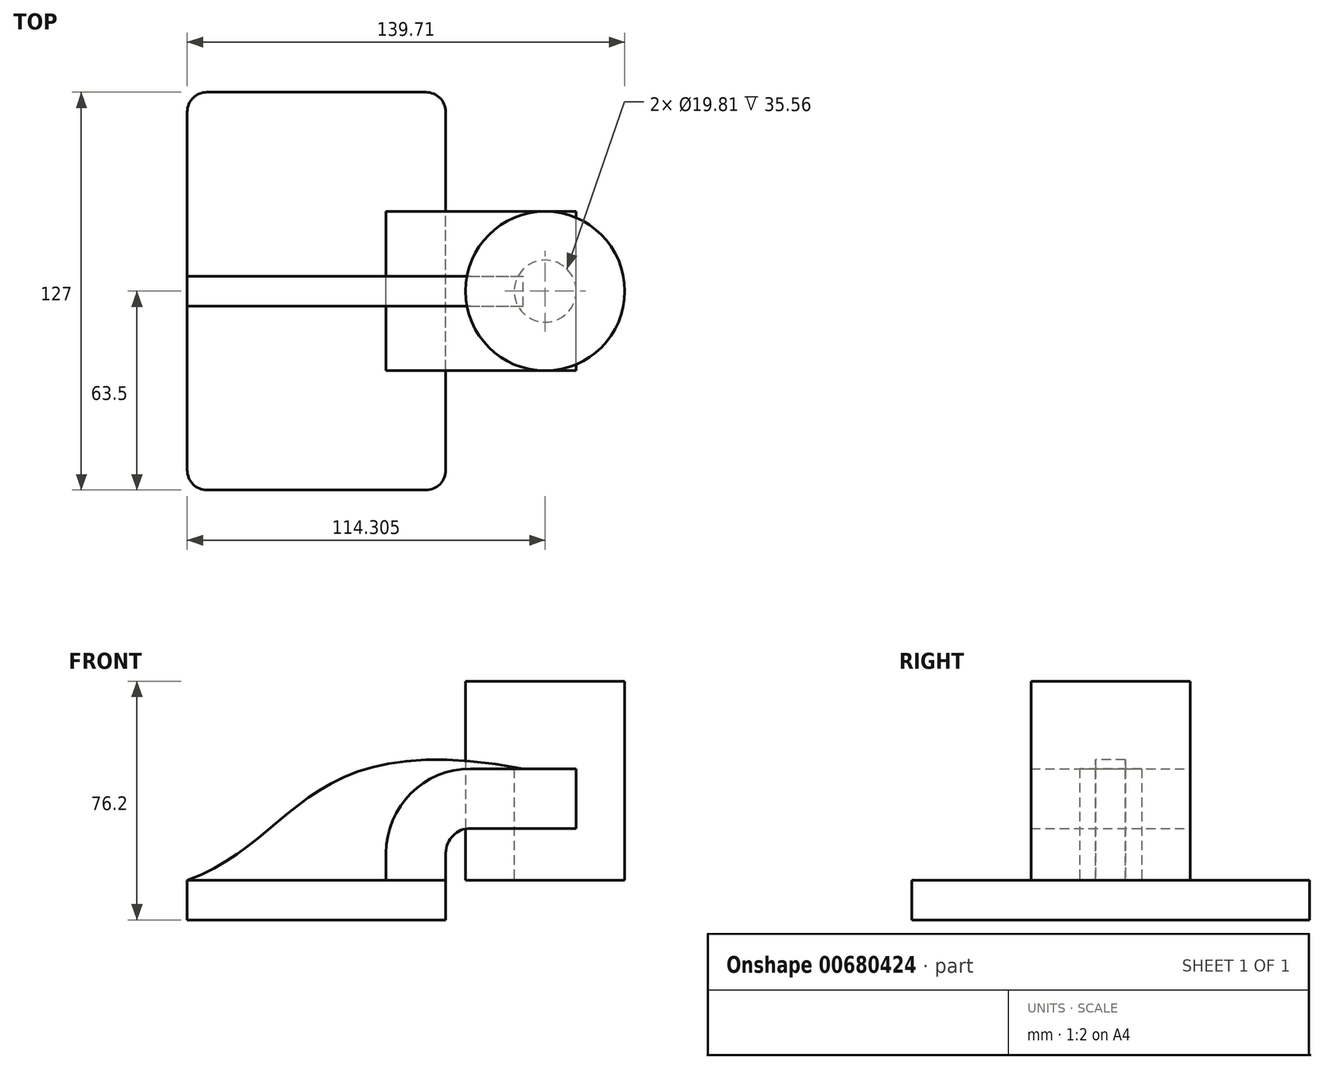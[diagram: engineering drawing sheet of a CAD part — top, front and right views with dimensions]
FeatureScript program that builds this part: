
annotation { "Feature Type Name" : "Feature", "Feature Type Description" : "" }
export const myFeature = defineFeature(function(context is Context, id is Id, definition is map)
    precondition{}
    {
        {
            var Q0;
            Q0=qCreatedBy(makeId("Front.planeOp"),FACE);
            var sketch = newSketch(context, id + "F0", { "sketchPlane" : qUnion([Q0])});
            skLineSegment(sketch, "E0.bottom", {"start": v(41.27, 6.35) * mm, "end": v(-41.28, 6.35) * mm});
            skLineSegment(sketch, "E0.top", {"start": v(41.28, -6.35) * mm, "end": v(-41.27, -6.35) * mm});
            skLineSegment(sketch, "E0.left", {"start": v(41.28, 6.35) * mm, "end": v(41.28, -6.35) * mm});
            skLineSegment(sketch, "E0.right", {"start": v(-41.28, 6.35) * mm, "end": v(-41.27, -6.35) * mm});
            skPoint(sketch, "E0.middle", {"position": v(0, 0) * mm});
            skLineSegment(sketch, "E1.bottom", {"start": v(98.42, 6.35) * mm, "end": v(73.03, 6.35) * mm});
            skLineSegment(sketch, "E1.top", {"start": v(98.42, 69.85) * mm, "end": v(73.02, 69.85) * mm});
            skLineSegment(sketch, "E1.left", {"start": v(98.42, 6.35) * mm, "end": v(98.42, 69.85) * mm});
            skLineSegment(sketch, "E1.right", {"start": v(73.03, 6.35) * mm, "end": v(73.03, 69.85) * mm});
            skPoint(sketch, "E1.middle", {"position": v(85.72, 38.1) * mm});
            skLineSegment(sketch, "E2", {"start": v(41.27, 6.35) * mm, "end": v(41.27, 14.95) * mm});
            skArc(sketch, "E3", {"start": v(49.18, 22.86) * mm, "mid": v(43.6, 20.54) * mm, "end": v(41.27, 14.95) * mm});
            skLineSegment(sketch, "E4", {"start": v(49.18, 22.86) * mm, "end": v(82.93, 22.86) * mm});
            skArc(sketch, "E5.1", {"start": v(49.18, 41.91) * mm, "mid": v(30.12, 34.01) * mm, "end": v(22.22, 14.95) * mm});
            skLineSegment(sketch, "E5.2", {"start": v(49.18, 41.91) * mm, "end": v(82.93, 41.91) * mm});
            skFitSpline(sketch, "E6", {"points": [v(-41.28, 6.35) * mm, v(66.06, 41.91) * mm], "startDerivative": vector(107.33, 38.1) * mm, "endDerivative": vector(213.02, -39.97) * mm});
            skLineSegment(sketch, "E7", {"start": v(22.22, 14.95) * mm, "end": v(22.22, 6.35) * mm});
            skLineSegment(sketch, "E8", {"start": v(82.93, 6.35) * mm, "end": v(82.93, 69.85) * mm});
            skSolve(sketch);
        }
        {
            var Q0;
            Q0=makeQuery(id+"F0.imprint","IMPRINT",FACE,{"disambiguationData":[TD([[makeQuery(id+"F0.imprint","IMPRINT",EDGE,{"derivedFrom":sQuery(id+"F0.wireOp",EDGE,"E0.top")}),-1.0]])]});
            extrude(context, id + "F1", {"entities" : qUnion([Q0]), "endBound" : BoundingType.SYMMETRIC, "depth" : 127 * mm, "offsetDistance" : 25.4 * mm});
        }
        {
            var Q0;
            {var subQ1=sQuery(id+"F0.wireOp",EDGE,"E5.1");Q0=makeQuery(id+"F0.imprint","IMPRINT",FACE,{"disambiguationData":[TD([[makeQuery(id+"F0.imprint","IMPRINT",EDGE,{"derivedFrom":subQ1}),-1.0]])]});}
            extrude(context, id + "F2", {"entities" : qUnion([Q0]), "endBound" : BoundingType.SYMMETRIC, "depth" : 9.52 * mm, "offsetDistance" : 25.4 * mm});
        }
        {
            var Q0;
            {var subQ0=sQuery(id+"F0.wireOp",EDGE,"E4");var subQ1=sQuery(id+"F0.wireOp",EDGE,"E1.right");var subQ2=makeQuery(id+"F0.imprint","INTERSECT",VERTEX,{"derivedFrom":[subQ1,subQ0]});Q0=makeQuery(id+"F0.imprint","IMPRINT",FACE,{"disambiguationData":[TD([[makeQuery(id+"F0.imprint","IMPRINT",EDGE,{"disambiguationData":[TD([[subQ2,-1.0]])],"derivedFrom":subQ1}),-1.0]])]});}
            var Q1;
            {var subQ1=sQuery(id+"F0.wireOp",EDGE,"E2");Q1=makeQuery(id+"F0.imprint","IMPRINT",FACE,{"disambiguationData":[TD([[makeQuery(id+"F0.imprint","IMPRINT",EDGE,{"derivedFrom":subQ1}),1.0]])]});}
            extrude(context, id + "F3", {"entities" : qUnion([Q0, Q1]), "endBound" : BoundingType.SYMMETRIC, "depth" : 50.8 * mm, "offsetDistance" : 25.4 * mm});
        }
        {
            var Q0;
            {var subQ4=sQuery(id+"F0.wireOp",EDGE,"E1.left");Q0=makeQuery(id+"F0.imprint","IMPRINT",FACE,{"disambiguationData":[TD([[makeQuery(id+"F0.imprint","IMPRINT",EDGE,{"derivedFrom":subQ4}),1.0]])]});}
            var Q1;
            {var subQ0=sQuery(id+"F0.wireOp",EDGE,"E1.right");var subQ1=sQuery(id+"F0.wireOp",EDGE,"E1.top");var subQ2=makeQuery(id+"F0.imprint","INTERSECT",VERTEX,{"derivedFrom":[subQ1,subQ0]});Q1=makeQuery(id+"F0.imprint","IMPRINT",FACE,{"disambiguationData":[TD([[makeQuery(id+"F0.imprint","IMPRINT",EDGE,{"disambiguationData":[TD([[subQ2,1.0]])],"derivedFrom":subQ1}),1.0]])]});}
            var Q2;
            Q2=sQuery(id+"F0.wireOp",EDGE,"E1.right");
            revolve(context, id + "F4", {"entities" : qUnion([Q0, Q1]), "axis" : qUnion([Q2]), "revolveType" : RevolveType.FULL});
        }
        {
            var Q0;
            Q0=makeQuery(id+"F1.opExtrude","CAP_EDGE",EDGE,{"disambiguationData":[OSD([sQuery(id+"F0.wireOp",EDGE,"E0.left")])],"isStart":false});
            var Q1;
            Q1=makeQuery(id+"F1.opExtrude","CAP_EDGE",EDGE,{"disambiguationData":[OSD([sQuery(id+"F0.wireOp",EDGE,"E0.right")])],"isStart":true});
            var Q2;
            Q2=makeQuery(id+"F1.opExtrude","CAP_EDGE",EDGE,{"disambiguationData":[OSD([sQuery(id+"F0.wireOp",EDGE,"E0.right")])],"isStart":false});
            var Q3;
            Q3=makeQuery(id+"F1.opExtrude","CAP_EDGE",EDGE,{"disambiguationData":[OSD([sQuery(id+"F0.wireOp",EDGE,"E0.left")])],"isStart":true});
            fillet(context, id + "F5", {"entities" : qUnion([Q0, Q1, Q2, Q3]), "radius" : 6.35 * mm, "tangentPropagation" : true, "allowEdgeOverflow" : false});
        }
    });
